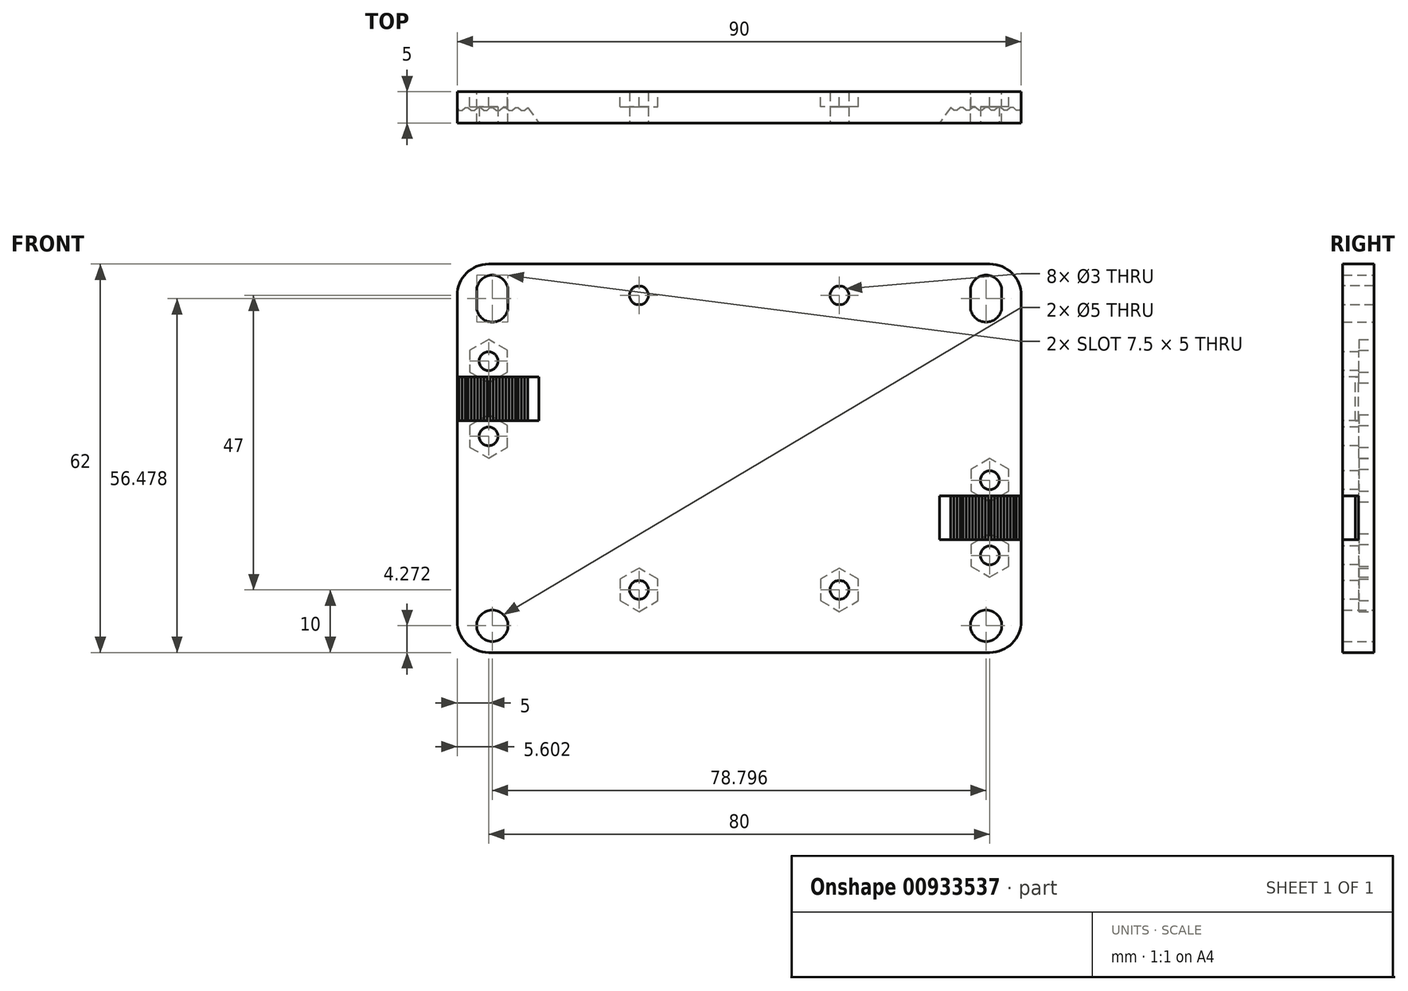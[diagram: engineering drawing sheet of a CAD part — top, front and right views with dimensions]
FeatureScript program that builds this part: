
annotation { "Feature Type Name" : "Feature", "Feature Type Description" : "" }
export const myFeature = defineFeature(function(context is Context, id is Id, definition is map)
    precondition{}
    {
        {
            var Q0;
            Q0=qCreatedBy(makeId("Front.planeOp"),FACE);
            var sketch = newSketch(context, id + "F0", { "sketchPlane" : qUnion([Q0])});
            skLineSegment(sketch, "E0.bottom", {"start": v(5, 0) * mm, "end": v(85, 0) * mm});
            skLineSegment(sketch, "E0.top", {"start": v(5, 62) * mm, "end": v(85, 62) * mm});
            skLineSegment(sketch, "E0.left", {"start": v(0, 5) * mm, "end": v(0, 57) * mm});
            skLineSegment(sketch, "E0.right", {"start": v(90, 5) * mm, "end": v(90, 57) * mm});
            skPoint(sketch, "E1.visualSharp", {"position": v(0, 62) * mm});
            skArc(sketch, "E1.filletArc", {"start": v(5, 62) * mm, "mid": v(1.46, 60.54) * mm, "end": v(0, 57) * mm});
            skPoint(sketch, "E2.visualSharp", {"position": v(90, 62) * mm});
            skArc(sketch, "E2.filletArc", {"start": v(90, 57) * mm, "mid": v(88.54, 60.54) * mm, "end": v(85, 62) * mm});
            skPoint(sketch, "E3.visualSharp", {"position": v(90, 0) * mm});
            skArc(sketch, "E3.filletArc", {"start": v(85, 0) * mm, "mid": v(88.54, 1.46) * mm, "end": v(90, 5) * mm});
            skPoint(sketch, "E4.visualSharp", {"position": v(0, 0) * mm});
            skArc(sketch, "E4.filletArc", {"start": v(0, 5) * mm, "mid": v(1.46, 1.46) * mm, "end": v(5, 0) * mm});
            skLineSegment(sketch, "E5", {"start": v(1.46, 60.54) * mm, "end": v(88.54, 1.46) * mm, "construction": true});
            skLineSegment(sketch, "E6", {"start": v(88.54, 1.46) * mm, "end": v(88.54, 60.54) * mm, "construction": true});
            skLineSegment(sketch, "E7", {"start": v(88.54, 60.54) * mm, "end": v(1.46, 1.46) * mm, "construction": true});
            skLineSegment(sketch, "E8", {"start": v(1.46, 1.46) * mm, "end": v(1.46, 60.54) * mm, "construction": true});
            skLineSegment(sketch, "E9", {"start": v(0, 31) * mm, "end": v(90, 31) * mm, "construction": true});
            skLineSegment(sketch, "E10", {"start": v(45, 62) * mm, "end": v(45, 0) * mm, "construction": true});
            skLineSegment(sketch, "E11", {"start": v(88.54, 60.54) * mm, "end": v(84.4, 57.73) * mm, "construction": true});
            skLineSegment(sketch, "E12", {"start": v(88.54, 1.46) * mm, "end": v(84.4, 4.27) * mm, "construction": true});
            skArc(sketch, "E13", {"start": v(86.9, 57.73) * mm, "mid": v(84.4, 60.23) * mm, "end": v(81.9, 57.73) * mm});
            skCircle(sketch, "E14", {"center": v(84.4, 4.27) * mm, "radius": 2.5 * mm});
            skCircle(sketch, "E15.MirrorC", {"center": v(5.6, 4.27) * mm, "radius": 2.5 * mm});
            skLineSegment(sketch, "E16", {"start": v(84.4, 57.73) * mm, "end": v(84.4, 55.23) * mm, "construction": true});
            skLineSegment(sketch, "E17", {"start": v(81.9, 57.73) * mm, "end": v(86.9, 57.73) * mm, "construction": true});
            skLineSegment(sketch, "E18", {"start": v(86.9, 55.23) * mm, "end": v(81.9, 55.23) * mm, "construction": true});
            skLineSegment(sketch, "E19", {"start": v(81.9, 57.73) * mm, "end": v(81.9, 55.23) * mm});
            skLineSegment(sketch, "E20", {"start": v(86.9, 57.73) * mm, "end": v(86.9, 55.23) * mm});
            skArc(sketch, "E21.trimOffspring", {"start": v(81.9, 55.23) * mm, "mid": v(84.4, 52.73) * mm, "end": v(86.9, 55.23) * mm});
            skLineSegment(sketch, "E22.MirrorCS", {"start": v(5.6, 57.73) * mm, "end": v(5.6, 55.23) * mm, "construction": true});
            skLineSegment(sketch, "E23.MirrorCS", {"start": v(3.1, 57.73) * mm, "end": v(3.1, 55.23) * mm});
            skArc(sketch, "E24.MirrorCS", {"start": v(8.1, 55.23) * mm, "mid": v(5.6, 52.73) * mm, "end": v(3.1, 55.23) * mm});
            skLineSegment(sketch, "E25.MirrorCS", {"start": v(8.1, 57.73) * mm, "end": v(3.1, 57.73) * mm, "construction": true});
            skArc(sketch, "E26.MirrorCS", {"start": v(3.1, 57.73) * mm, "mid": v(5.6, 60.23) * mm, "end": v(8.1, 57.73) * mm});
            skLineSegment(sketch, "E27.MirrorCS", {"start": v(8.1, 57.73) * mm, "end": v(8.1, 55.23) * mm});
            skLineSegment(sketch, "E28.MirrorCS", {"start": v(3.1, 55.23) * mm, "end": v(8.1, 55.23) * mm, "construction": true});
            skSolve(sketch);
        }
        {
            var Q0;
            Q0=makeQuery(id+"F0.imprint","IMPRINT",FACE,{"disambiguationData":[TD([[makeQuery(id+"F0.imprint","IMPRINT",EDGE,{"derivedFrom":sQuery(id+"F0.wireOp",EDGE,"E0.bottom")}),1.0]])]});
            extrude(context, id + "F1", {"entities" : qUnion([Q0]), "depth" : 5 * mm, "offsetDistance" : 25 * mm});
        }
        {
            var Q0;
            Q0=makeQuery(id+"F1.opExtrude","CAP_FACE",FACE,{"disambiguationData":[OSD([sQuery(id+"F0.wireOp",EDGE,"E0.bottom"),sQuery(id+"F0.wireOp",EDGE,"E0.top"),sQuery(id+"F0.wireOp",EDGE,"E0.left"),sQuery(id+"F0.wireOp",EDGE,"E0.right"),sQuery(id+"F0.wireOp",EDGE,"E1.filletArc"),sQuery(id+"F0.wireOp",EDGE,"E2.filletArc"),sQuery(id+"F0.wireOp",EDGE,"E3.filletArc"),sQuery(id+"F0.wireOp",EDGE,"E4.filletArc"),sQuery(id+"F0.wireOp",EDGE,"E13"),sQuery(id+"F0.wireOp",EDGE,"E14"),sQuery(id+"F0.wireOp",EDGE,"E15.MirrorC"),sQuery(id+"F0.wireOp",EDGE,"E19"),sQuery(id+"F0.wireOp",EDGE,"E20"),sQuery(id+"F0.wireOp",EDGE,"E21.trimOffspring"),sQuery(id+"F0.wireOp",EDGE,"E23.MirrorCS"),sQuery(id+"F0.wireOp",EDGE,"E24.MirrorCS"),sQuery(id+"F0.wireOp",EDGE,"E26.MirrorCS"),sQuery(id+"F0.wireOp",EDGE,"E27.MirrorCS")])],"isStart":false});
            var sketch = newSketch(context, id + "F2", { "sketchPlane" : qUnion([Q0])});
            skLineSegment(sketch, "E29", {"start": v(9.26, 62) * mm, "end": v(9.26, 44) * mm, "construction": true});
            skLineSegment(sketch, "E30", {"start": v(81.08, 0) * mm, "end": v(81.08, 18) * mm, "construction": true});
            skLineSegment(sketch, "E31.bottom", {"start": v(90, 18) * mm, "end": v(77, 18) * mm});
            skLineSegment(sketch, "E31.top", {"start": v(90, 25) * mm, "end": v(77, 25) * mm});
            skLineSegment(sketch, "E31.left", {"start": v(90, 18) * mm, "end": v(90, 25) * mm});
            skLineSegment(sketch, "E31.right", {"start": v(77, 18) * mm, "end": v(77, 25) * mm});
            skLineSegment(sketch, "E32.bottom", {"start": v(0, 44) * mm, "end": v(13, 44) * mm});
            skLineSegment(sketch, "E32.top", {"start": v(0, 37) * mm, "end": v(13, 37) * mm});
            skLineSegment(sketch, "E32.left", {"start": v(0, 44) * mm, "end": v(0, 37) * mm});
            skLineSegment(sketch, "E32.right", {"start": v(13, 44) * mm, "end": v(13, 37) * mm});
            skSolve(sketch);
        }
        {
            var Q0;
            Q0=makeQuery(id+"F2.imprint","IMPRINT",FACE,{"disambiguationData":[TD([[makeQuery(id+"F2.imprint","IMPRINT",EDGE,{"derivedFrom":sQuery(id+"F2.wireOp",EDGE,"E32.bottom")}),-1.0]])]});
            var Q1;
            Q1=makeQuery(id+"F2.imprint","IMPRINT",FACE,{"disambiguationData":[TD([[makeQuery(id+"F2.imprint","IMPRINT",EDGE,{"derivedFrom":sQuery(id+"F2.wireOp",EDGE,"E31.bottom")}),-1.0]])]});
            extrude(context, id + "F3", {"entities" : qUnion([Q0, Q1]), "operationType" : NewBodyOperationType.REMOVE, "oppositeDirection" : true, "depth" : 2.5 * mm, "offsetDistance" : 25 * mm});
        }
        {
            var Q0;
            Q0=makeQuery(id+"F3.boolean.opBoolean","COPY",FACE,{"derivedFrom":makeQuery(id+"F3.opExtrude","SWEPT_FACE",FACE,{"disambiguationData":[OSD([sQuery(id+"F2.wireOp",EDGE,"E32.bottom")])]})});
            var sketch = newSketch(context, id + "F4", { "sketchPlane" : qUnion([Q0])});
            skLineSegment(sketch, "E33", {"start": v(0, 2.5) * mm, "end": v(0, 3) * mm, "construction": true});
            skLineSegment(sketch, "E34", {"start": v(0, 3) * mm, "end": v(0.25, 3) * mm, "construction": true});
            skLineSegment(sketch, "E35", {"start": v(0.25, 3) * mm, "end": v(0.75, 3) * mm, "construction": true});
            skLineSegment(sketch, "E36", {"start": v(0.75, 3) * mm, "end": v(1.25, 3) * mm, "construction": true});
            skLineSegment(sketch, "E37", {"start": v(1.25, 3) * mm, "end": v(1.75, 3) * mm, "construction": true});
            skLineSegment(sketch, "E38", {"start": v(0, 2.5) * mm, "end": v(0.25, 3) * mm});
            skLineSegment(sketch, "E39", {"start": v(0.25, 3) * mm, "end": v(0.75, 3) * mm});
            skLineSegment(sketch, "E40", {"start": v(0.75, 3) * mm, "end": v(1.25, 2.5) * mm});
            skLineSegment(sketch, "E41", {"start": v(1.75, 3) * mm, "end": v(2.25, 3) * mm, "construction": true});
            skLineSegment(sketch, "E42", {"start": v(2.25, 3) * mm, "end": v(2.75, 3) * mm, "construction": true});
            skLineSegment(sketch, "E43", {"start": v(2.75, 3) * mm, "end": v(3.25, 3) * mm, "construction": true});
            skLineSegment(sketch, "E44", {"start": v(3.25, 3) * mm, "end": v(3.75, 3) * mm, "construction": true});
            skLineSegment(sketch, "E45", {"start": v(3.75, 3) * mm, "end": v(4.25, 3) * mm, "construction": true});
            skLineSegment(sketch, "E46", {"start": v(4.25, 3) * mm, "end": v(4.75, 3) * mm, "construction": true});
            skLineSegment(sketch, "E47", {"start": v(4.75, 3) * mm, "end": v(5.25, 3) * mm, "construction": true});
            skLineSegment(sketch, "E48", {"start": v(5.25, 3) * mm, "end": v(5.75, 3) * mm, "construction": true});
            skLineSegment(sketch, "E49", {"start": v(5.75, 3) * mm, "end": v(6.25, 3) * mm, "construction": true});
            skLineSegment(sketch, "E50", {"start": v(6.25, 3) * mm, "end": v(6.75, 3) * mm, "construction": true});
            skLineSegment(sketch, "E51", {"start": v(6.75, 3) * mm, "end": v(7.25, 3) * mm, "construction": true});
            skLineSegment(sketch, "E52", {"start": v(7.25, 3) * mm, "end": v(7.75, 3) * mm, "construction": true});
            skLineSegment(sketch, "E53", {"start": v(7.75, 3) * mm, "end": v(8.25, 3) * mm, "construction": true});
            skLineSegment(sketch, "E54", {"start": v(8.25, 3) * mm, "end": v(8.75, 3) * mm, "construction": true});
            skLineSegment(sketch, "E55", {"start": v(8.75, 3) * mm, "end": v(9.25, 3) * mm, "construction": true});
            skLineSegment(sketch, "E56", {"start": v(9.25, 3) * mm, "end": v(9.75, 3) * mm, "construction": true});
            skLineSegment(sketch, "E57", {"start": v(9.75, 3) * mm, "end": v(10.25, 3) * mm, "construction": true});
            skLineSegment(sketch, "E58", {"start": v(10.25, 3) * mm, "end": v(10.75, 3) * mm, "construction": true});
            skLineSegment(sketch, "E59", {"start": v(10.75, 3) * mm, "end": v(11.25, 3) * mm, "construction": true});
            skLineSegment(sketch, "E60", {"start": v(11.25, 3) * mm, "end": v(11.75, 3) * mm, "construction": true});
            skLineSegment(sketch, "E61", {"start": v(1.25, 2.5) * mm, "end": v(1.75, 2.5) * mm});
            skLineSegment(sketch, "E62", {"start": v(1.75, 2.5) * mm, "end": v(2.25, 3) * mm});
            skLineSegment(sketch, "E63", {"start": v(2.25, 3) * mm, "end": v(2.75, 3) * mm});
            skLineSegment(sketch, "E64", {"start": v(2.75, 3) * mm, "end": v(3.25, 2.5) * mm});
            skLineSegment(sketch, "E65", {"start": v(3.25, 2.5) * mm, "end": v(3.75, 2.5) * mm});
            skLineSegment(sketch, "E66", {"start": v(3.75, 2.5) * mm, "end": v(4.25, 3) * mm});
            skLineSegment(sketch, "E67", {"start": v(4.25, 3) * mm, "end": v(4.75, 3) * mm});
            skLineSegment(sketch, "E68", {"start": v(4.75, 3) * mm, "end": v(5.25, 2.5) * mm});
            skLineSegment(sketch, "E69", {"start": v(5.25, 2.5) * mm, "end": v(5.75, 2.5) * mm});
            skLineSegment(sketch, "E70", {"start": v(5.75, 2.5) * mm, "end": v(6.25, 3) * mm});
            skLineSegment(sketch, "E71", {"start": v(6.25, 3) * mm, "end": v(6.75, 3) * mm});
            skLineSegment(sketch, "E72", {"start": v(6.75, 3) * mm, "end": v(7.25, 2.5) * mm});
            skLineSegment(sketch, "E73", {"start": v(7.25, 2.5) * mm, "end": v(7.75, 2.5) * mm});
            skLineSegment(sketch, "E74", {"start": v(7.75, 2.5) * mm, "end": v(8.25, 3) * mm});
            skLineSegment(sketch, "E75", {"start": v(8.25, 3) * mm, "end": v(8.75, 3) * mm});
            skLineSegment(sketch, "E76", {"start": v(8.75, 3) * mm, "end": v(9.25, 2.5) * mm});
            skLineSegment(sketch, "E77", {"start": v(9.25, 2.5) * mm, "end": v(9.75, 2.5) * mm});
            skLineSegment(sketch, "E78", {"start": v(9.75, 2.5) * mm, "end": v(10.25, 3) * mm});
            skLineSegment(sketch, "E79", {"start": v(10.25, 3) * mm, "end": v(10.75, 3) * mm});
            skLineSegment(sketch, "E80", {"start": v(10.75, 3) * mm, "end": v(11.25, 2.5) * mm});
            skLineSegment(sketch, "E81", {"start": v(11.25, 2.5) * mm, "end": v(13, 5) * mm});
            skSolve(sketch);
        }
        {
            var Q0;
            {var subQ0=sQuery(id+"F4.wireOp",EDGE,"E81");Q0=makeQuery(id+"F4.imprint","IMPRINT",FACE,{"disambiguationData":[TD([[makeQuery(id+"F4.imprint","IMPRINT",EDGE,{"derivedFrom":subQ0}),-1.0]])]});}
            var Q1;
            {var subQ0=sQuery(id+"F4.wireOp",EDGE,"E74");Q1=makeQuery(id+"F4.imprint","IMPRINT",FACE,{"disambiguationData":[TD([[makeQuery(id+"F4.imprint","IMPRINT",EDGE,{"derivedFrom":subQ0}),-1.0]])]});}
            var Q2;
            {var subQ0=sQuery(id+"F4.wireOp",EDGE,"E78");Q2=makeQuery(id+"F4.imprint","IMPRINT",FACE,{"disambiguationData":[TD([[makeQuery(id+"F4.imprint","IMPRINT",EDGE,{"derivedFrom":subQ0}),-1.0]])]});}
            var Q3;
            {var subQ0=sQuery(id+"F4.wireOp",EDGE,"E70");Q3=makeQuery(id+"F4.imprint","IMPRINT",FACE,{"disambiguationData":[TD([[makeQuery(id+"F4.imprint","IMPRINT",EDGE,{"derivedFrom":subQ0}),-1.0]])]});}
            var Q4;
            {var subQ0=sQuery(id+"F4.wireOp",EDGE,"E66");Q4=makeQuery(id+"F4.imprint","IMPRINT",FACE,{"disambiguationData":[TD([[makeQuery(id+"F4.imprint","IMPRINT",EDGE,{"derivedFrom":subQ0}),-1.0]])]});}
            var Q5;
            {var subQ0=sQuery(id+"F4.wireOp",EDGE,"E62");Q5=makeQuery(id+"F4.imprint","IMPRINT",FACE,{"disambiguationData":[TD([[makeQuery(id+"F4.imprint","IMPRINT",EDGE,{"derivedFrom":subQ0}),-1.0]])]});}
            var Q6;
            {var subQ0=sQuery(id+"F4.wireOp",EDGE,"E38");Q6=makeQuery(id+"F4.imprint","IMPRINT",FACE,{"disambiguationData":[TD([[makeQuery(id+"F4.imprint","IMPRINT",EDGE,{"derivedFrom":subQ0}),-1.0]])]});}
            extrude(context, id + "F5", {"entities" : qUnion([Q0, Q1, Q2, Q3, Q4, Q5, Q6]), "operationType" : NewBodyOperationType.ADD, "endBound" : BoundingType.UP_TO_NEXT, "depth" : 25 * mm, "offsetDistance" : 25 * mm});
        }
        {
            var Q0;
            Q0=makeQuery(id+"F3.boolean.opBoolean","COPY",FACE,{"derivedFrom":makeQuery(id+"F3.opExtrude","SWEPT_FACE",FACE,{"disambiguationData":[OSD([sQuery(id+"F2.wireOp",EDGE,"E31.bottom")])]})});
            var sketch = newSketch(context, id + "F6", { "sketchPlane" : qUnion([Q0])});
            skLineSegment(sketch, "E82", {"start": v(90, -2.5) * mm, "end": v(90, -3) * mm, "construction": true});
            skLineSegment(sketch, "E83", {"start": v(90, -3) * mm, "end": v(89.75, -3) * mm, "construction": true});
            skLineSegment(sketch, "E84", {"start": v(89.75, -3) * mm, "end": v(89.25, -3) * mm, "construction": true});
            skLineSegment(sketch, "E85", {"start": v(89.25, -3) * mm, "end": v(88.75, -3) * mm, "construction": true});
            skLineSegment(sketch, "E86", {"start": v(88.75, -3) * mm, "end": v(88.25, -3) * mm, "construction": true});
            skLineSegment(sketch, "E87", {"start": v(88.25, -3) * mm, "end": v(87.75, -3) * mm, "construction": true});
            skLineSegment(sketch, "E88", {"start": v(87.75, -3) * mm, "end": v(87.25, -3) * mm, "construction": true});
            skLineSegment(sketch, "E89", {"start": v(87.25, -3) * mm, "end": v(86.75, -3) * mm, "construction": true});
            skLineSegment(sketch, "E90", {"start": v(86.75, -3) * mm, "end": v(86.25, -3) * mm, "construction": true});
            skLineSegment(sketch, "E91", {"start": v(86.25, -3) * mm, "end": v(85.75, -3) * mm, "construction": true});
            skLineSegment(sketch, "E92", {"start": v(85.75, -3) * mm, "end": v(85.25, -3) * mm, "construction": true});
            skLineSegment(sketch, "E93", {"start": v(85.25, -3) * mm, "end": v(84.75, -3) * mm, "construction": true});
            skLineSegment(sketch, "E94", {"start": v(84.75, -3) * mm, "end": v(84.25, -3) * mm, "construction": true});
            skLineSegment(sketch, "E95", {"start": v(84.25, -3) * mm, "end": v(83.75, -3) * mm, "construction": true});
            skLineSegment(sketch, "E96", {"start": v(83.75, -3) * mm, "end": v(83.25, -3) * mm, "construction": true});
            skLineSegment(sketch, "E97", {"start": v(83.25, -3) * mm, "end": v(82.75, -3) * mm, "construction": true});
            skLineSegment(sketch, "E98", {"start": v(82.75, -3) * mm, "end": v(82.25, -3) * mm, "construction": true});
            skLineSegment(sketch, "E99", {"start": v(82.25, -3) * mm, "end": v(81.75, -3) * mm, "construction": true});
            skLineSegment(sketch, "E100", {"start": v(81.75, -3) * mm, "end": v(81.25, -3) * mm, "construction": true});
            skLineSegment(sketch, "E101", {"start": v(81.25, -3) * mm, "end": v(80.75, -3) * mm, "construction": true});
            skLineSegment(sketch, "E102", {"start": v(80.75, -3) * mm, "end": v(80.25, -3) * mm, "construction": true});
            skLineSegment(sketch, "E103", {"start": v(80.25, -3) * mm, "end": v(79.75, -3) * mm, "construction": true});
            skLineSegment(sketch, "E104", {"start": v(79.75, -3) * mm, "end": v(79.25, -3) * mm, "construction": true});
            skLineSegment(sketch, "E105", {"start": v(79.25, -3) * mm, "end": v(78.75, -3) * mm, "construction": true});
            skLineSegment(sketch, "E106", {"start": v(78.75, -3) * mm, "end": v(78.25, -3) * mm, "construction": true});
            skLineSegment(sketch, "E107", {"start": v(78.25, -3) * mm, "end": v(77.75, -3) * mm, "construction": true});
            skLineSegment(sketch, "E108", {"start": v(90, -2.5) * mm, "end": v(89.75, -3) * mm});
            skLineSegment(sketch, "E109", {"start": v(89.75, -3) * mm, "end": v(89.25, -3) * mm});
            skLineSegment(sketch, "E110", {"start": v(89.25, -3) * mm, "end": v(88.75, -2.5) * mm});
            skLineSegment(sketch, "E111", {"start": v(88.75, -2.5) * mm, "end": v(88.25, -2.5) * mm});
            skLineSegment(sketch, "E112", {"start": v(88.25, -2.5) * mm, "end": v(87.75, -3) * mm});
            skLineSegment(sketch, "E113", {"start": v(87.75, -3) * mm, "end": v(87.25, -3) * mm});
            skLineSegment(sketch, "E114", {"start": v(87.25, -3) * mm, "end": v(86.75, -2.5) * mm});
            skLineSegment(sketch, "E115", {"start": v(86.75, -2.5) * mm, "end": v(86.25, -2.5) * mm});
            skLineSegment(sketch, "E116", {"start": v(86.25, -2.5) * mm, "end": v(85.75, -3) * mm});
            skLineSegment(sketch, "E117", {"start": v(85.75, -3) * mm, "end": v(85.25, -3) * mm});
            skLineSegment(sketch, "E118", {"start": v(85.25, -3) * mm, "end": v(84.75, -2.5) * mm});
            skLineSegment(sketch, "E119", {"start": v(84.75, -2.5) * mm, "end": v(84.25, -2.5) * mm});
            skLineSegment(sketch, "E120", {"start": v(84.25, -2.5) * mm, "end": v(83.75, -3) * mm});
            skLineSegment(sketch, "E121", {"start": v(83.75, -3) * mm, "end": v(83.25, -3) * mm});
            skLineSegment(sketch, "E122", {"start": v(83.25, -3) * mm, "end": v(82.75, -2.5) * mm});
            skLineSegment(sketch, "E123", {"start": v(82.75, -2.5) * mm, "end": v(82.25, -2.5) * mm});
            skLineSegment(sketch, "E124", {"start": v(82.25, -2.5) * mm, "end": v(81.75, -3) * mm});
            skLineSegment(sketch, "E125", {"start": v(81.75, -3) * mm, "end": v(81.25, -3) * mm});
            skLineSegment(sketch, "E126", {"start": v(81.25, -3) * mm, "end": v(80.75, -2.5) * mm});
            skLineSegment(sketch, "E127", {"start": v(80.75, -2.5) * mm, "end": v(80.25, -2.5) * mm});
            skLineSegment(sketch, "E128", {"start": v(80.25, -2.5) * mm, "end": v(79.75, -3) * mm});
            skLineSegment(sketch, "E129", {"start": v(79.75, -3) * mm, "end": v(79.25, -3) * mm});
            skLineSegment(sketch, "E130", {"start": v(79.25, -3) * mm, "end": v(78.75, -2.5) * mm});
            skLineSegment(sketch, "E131", {"start": v(78.75, -2.5) * mm, "end": v(77, -5) * mm});
            skSolve(sketch);
        }
        {
            var Q0;
            {var subQ0=sQuery(id+"F6.wireOp",EDGE,"E131");Q0=makeQuery(id+"F6.imprint","IMPRINT",FACE,{"disambiguationData":[TD([[makeQuery(id+"F6.imprint","IMPRINT",EDGE,{"derivedFrom":subQ0}),-1.0]])]});}
            var Q1;
            {var subQ0=sQuery(id+"F6.wireOp",EDGE,"E128");Q1=makeQuery(id+"F6.imprint","IMPRINT",FACE,{"disambiguationData":[TD([[makeQuery(id+"F6.imprint","IMPRINT",EDGE,{"derivedFrom":subQ0}),-1.0]])]});}
            var Q2;
            {var subQ0=sQuery(id+"F6.wireOp",EDGE,"E124");Q2=makeQuery(id+"F6.imprint","IMPRINT",FACE,{"disambiguationData":[TD([[makeQuery(id+"F6.imprint","IMPRINT",EDGE,{"derivedFrom":subQ0}),-1.0]])]});}
            var Q3;
            {var subQ0=sQuery(id+"F6.wireOp",EDGE,"E120");Q3=makeQuery(id+"F6.imprint","IMPRINT",FACE,{"disambiguationData":[TD([[makeQuery(id+"F6.imprint","IMPRINT",EDGE,{"derivedFrom":subQ0}),-1.0]])]});}
            var Q4;
            {var subQ0=sQuery(id+"F6.wireOp",EDGE,"E116");Q4=makeQuery(id+"F6.imprint","IMPRINT",FACE,{"disambiguationData":[TD([[makeQuery(id+"F6.imprint","IMPRINT",EDGE,{"derivedFrom":subQ0}),-1.0]])]});}
            var Q5;
            {var subQ0=sQuery(id+"F6.wireOp",EDGE,"E112");Q5=makeQuery(id+"F6.imprint","IMPRINT",FACE,{"disambiguationData":[TD([[makeQuery(id+"F6.imprint","IMPRINT",EDGE,{"derivedFrom":subQ0}),-1.0]])]});}
            var Q6;
            {var subQ0=sQuery(id+"F6.wireOp",EDGE,"E108");Q6=makeQuery(id+"F6.imprint","IMPRINT",FACE,{"disambiguationData":[TD([[makeQuery(id+"F6.imprint","IMPRINT",EDGE,{"derivedFrom":subQ0}),-1.0]])]});}
            extrude(context, id + "F7", {"entities" : qUnion([Q0, Q1, Q2, Q3, Q4, Q5, Q6]), "operationType" : NewBodyOperationType.ADD, "endBound" : BoundingType.UP_TO_NEXT, "depth" : 25 * mm, "offsetDistance" : 25 * mm});
        }
        {
            var Q0;
            Q0=makeQuery(id+"F1.opExtrude","CAP_FACE",FACE,{"disambiguationData":[OSD([sQuery(id+"F0.wireOp",EDGE,"E0.bottom"),sQuery(id+"F0.wireOp",EDGE,"E0.top"),sQuery(id+"F0.wireOp",EDGE,"E0.left"),sQuery(id+"F0.wireOp",EDGE,"E0.right"),sQuery(id+"F0.wireOp",EDGE,"E1.filletArc"),sQuery(id+"F0.wireOp",EDGE,"E2.filletArc"),sQuery(id+"F0.wireOp",EDGE,"E3.filletArc"),sQuery(id+"F0.wireOp",EDGE,"E4.filletArc"),sQuery(id+"F0.wireOp",EDGE,"E13"),sQuery(id+"F0.wireOp",EDGE,"E14"),sQuery(id+"F0.wireOp",EDGE,"E15.MirrorC"),sQuery(id+"F0.wireOp",EDGE,"E19"),sQuery(id+"F0.wireOp",EDGE,"E20"),sQuery(id+"F0.wireOp",EDGE,"E21.trimOffspring"),sQuery(id+"F0.wireOp",EDGE,"E23.MirrorCS"),sQuery(id+"F0.wireOp",EDGE,"E24.MirrorCS"),sQuery(id+"F0.wireOp",EDGE,"E26.MirrorCS"),sQuery(id+"F0.wireOp",EDGE,"E27.MirrorCS")])],"isStart":false});
            var sketch = newSketch(context, id + "F8", { "sketchPlane" : qUnion([Q0])});
            skLineSegment(sketch, "E132", {"start": v(90, 29.82) * mm, "end": v(85, 29.82) * mm, "construction": true});
            skLineSegment(sketch, "E133", {"start": v(85, 25) * mm, "end": v(85, 27.5) * mm, "construction": true});
            skLineSegment(sketch, "E134", {"start": v(85, 18) * mm, "end": v(85, 15.5) * mm, "construction": true});
            skCircle(sketch, "E135", {"center": v(85, 27.5) * mm, "radius": 1.5 * mm});
            skCircle(sketch, "E136", {"center": v(85, 15.5) * mm, "radius": 1.5 * mm});
            skLineSegment(sketch, "E137", {"start": v(0, 51.21) * mm, "end": v(5, 51.21) * mm, "construction": true});
            skLineSegment(sketch, "E138", {"start": v(5, 44) * mm, "end": v(5, 46.5) * mm, "construction": true});
            skLineSegment(sketch, "E139", {"start": v(5, 37) * mm, "end": v(5, 34.5) * mm, "construction": true});
            skCircle(sketch, "E140", {"center": v(5, 46.5) * mm, "radius": 1.5 * mm});
            skCircle(sketch, "E141", {"center": v(5, 34.5) * mm, "radius": 1.5 * mm});
            skSolve(sketch);
        }
        {
            var Q0;
            Q0=makeQuery(id+"F8.imprint","IMPRINT",FACE,{"disambiguationData":[TD([[makeQuery(id+"F8.imprint","IMPRINT",EDGE,{"derivedFrom":sQuery(id+"F8.wireOp",EDGE,"E140")}),1.0]])]});
            var Q1;
            Q1=makeQuery(id+"F8.imprint","IMPRINT",FACE,{"disambiguationData":[TD([[makeQuery(id+"F8.imprint","IMPRINT",EDGE,{"derivedFrom":sQuery(id+"F8.wireOp",EDGE,"E141")}),1.0]])]});
            var Q2;
            Q2=makeQuery(id+"F8.imprint","IMPRINT",FACE,{"disambiguationData":[TD([[makeQuery(id+"F8.imprint","IMPRINT",EDGE,{"derivedFrom":sQuery(id+"F8.wireOp",EDGE,"E135")}),1.0]])]});
            var Q3;
            Q3=makeQuery(id+"F8.imprint","IMPRINT",FACE,{"disambiguationData":[TD([[makeQuery(id+"F8.imprint","IMPRINT",EDGE,{"derivedFrom":sQuery(id+"F8.wireOp",EDGE,"E136")}),1.0]])]});
            extrude(context, id + "F9", {"entities" : qUnion([Q0, Q1, Q2, Q3]), "operationType" : NewBodyOperationType.REMOVE, "oppositeDirection" : true, "depth" : 5 * mm, "offsetDistance" : 25 * mm});
        }
        {
            var Q0;
            Q0=makeQuery(id+"F1.opExtrude","CAP_FACE",FACE,{"disambiguationData":[OSD([sQuery(id+"F0.wireOp",EDGE,"E0.bottom"),sQuery(id+"F0.wireOp",EDGE,"E0.top"),sQuery(id+"F0.wireOp",EDGE,"E0.left"),sQuery(id+"F0.wireOp",EDGE,"E0.right"),sQuery(id+"F0.wireOp",EDGE,"E1.filletArc"),sQuery(id+"F0.wireOp",EDGE,"E2.filletArc"),sQuery(id+"F0.wireOp",EDGE,"E3.filletArc"),sQuery(id+"F0.wireOp",EDGE,"E4.filletArc"),sQuery(id+"F0.wireOp",EDGE,"E13"),sQuery(id+"F0.wireOp",EDGE,"E14"),sQuery(id+"F0.wireOp",EDGE,"E15.MirrorC"),sQuery(id+"F0.wireOp",EDGE,"E19"),sQuery(id+"F0.wireOp",EDGE,"E20"),sQuery(id+"F0.wireOp",EDGE,"E21.trimOffspring"),sQuery(id+"F0.wireOp",EDGE,"E23.MirrorCS"),sQuery(id+"F0.wireOp",EDGE,"E24.MirrorCS"),sQuery(id+"F0.wireOp",EDGE,"E26.MirrorCS"),sQuery(id+"F0.wireOp",EDGE,"E27.MirrorCS")])],"isStart":true});
            var sketch = newSketch(context, id + "F10", { "sketchPlane" : qUnion([Q0])});
            skLineSegment(sketch, "E142", {"start": v(-85, 27.5) * mm, "end": v(-82, 27.5) * mm, "construction": true});
            skLineSegment(sketch, "E143", {"start": v(-85, 15.5) * mm, "end": v(-82, 15.5) * mm, "construction": true});
            skLineSegment(sketch, "E144", {"start": v(-5, 46.5) * mm, "end": v(-8, 46.5) * mm, "construction": true});
            skLineSegment(sketch, "E145", {"start": v(-5, 34.5) * mm, "end": v(-8, 34.5) * mm, "construction": true});
            skCircle(sketch, "E146.cCircle", {"center": v(-5, 46.5) * mm, "radius": 3 * mm, "construction": true});
            skLineSegment(sketch, "E146.0", {"start": v(-8, 44.77) * mm, "end": v(-8, 48.23) * mm});
            skLineSegment(sketch, "E146.1", {"start": v(-8, 48.23) * mm, "end": v(-5, 49.96) * mm});
            skLineSegment(sketch, "E146.2", {"start": v(-5, 49.96) * mm, "end": v(-2, 48.23) * mm});
            skLineSegment(sketch, "E146.3", {"start": v(-2, 48.23) * mm, "end": v(-2, 44.77) * mm});
            skLineSegment(sketch, "E146.4", {"start": v(-2, 44.77) * mm, "end": v(-5, 43.04) * mm});
            skLineSegment(sketch, "E146.5", {"start": v(-5, 43.04) * mm, "end": v(-8, 44.77) * mm});
            skPoint(sketch, "E146.0.midPoint", {"position": v(-8, 46.5) * mm});
            skCircle(sketch, "E147.cCircle", {"center": v(-5, 34.5) * mm, "radius": 3 * mm, "construction": true});
            skLineSegment(sketch, "E147.0", {"start": v(-8, 32.77) * mm, "end": v(-8, 36.23) * mm});
            skLineSegment(sketch, "E147.1", {"start": v(-8, 36.23) * mm, "end": v(-5, 37.96) * mm});
            skLineSegment(sketch, "E147.2", {"start": v(-5, 37.96) * mm, "end": v(-2, 36.23) * mm});
            skLineSegment(sketch, "E147.3", {"start": v(-2, 36.23) * mm, "end": v(-2, 32.77) * mm});
            skLineSegment(sketch, "E147.4", {"start": v(-2, 32.77) * mm, "end": v(-5, 31.04) * mm});
            skLineSegment(sketch, "E147.5", {"start": v(-5, 31.04) * mm, "end": v(-8, 32.77) * mm});
            skPoint(sketch, "E147.0.midPoint", {"position": v(-8, 34.5) * mm});
            skCircle(sketch, "E148.cCircle", {"center": v(-85, 27.5) * mm, "radius": 3 * mm, "construction": true});
            skLineSegment(sketch, "E148.0", {"start": v(-82, 29.23) * mm, "end": v(-82, 25.77) * mm});
            skLineSegment(sketch, "E148.1", {"start": v(-82, 25.77) * mm, "end": v(-85, 24.04) * mm});
            skLineSegment(sketch, "E148.2", {"start": v(-85, 24.04) * mm, "end": v(-88, 25.77) * mm});
            skLineSegment(sketch, "E148.3", {"start": v(-88, 25.77) * mm, "end": v(-88, 29.23) * mm});
            skLineSegment(sketch, "E148.4", {"start": v(-88, 29.23) * mm, "end": v(-85, 30.96) * mm});
            skLineSegment(sketch, "E148.5", {"start": v(-85, 30.96) * mm, "end": v(-82, 29.23) * mm});
            skPoint(sketch, "E148.0.midPoint", {"position": v(-82, 27.5) * mm});
            skCircle(sketch, "E149.cCircle", {"center": v(-85, 15.5) * mm, "radius": 3 * mm, "construction": true});
            skLineSegment(sketch, "E149.0", {"start": v(-82, 17.23) * mm, "end": v(-82, 13.77) * mm});
            skLineSegment(sketch, "E149.1", {"start": v(-82, 13.77) * mm, "end": v(-85, 12.04) * mm});
            skLineSegment(sketch, "E149.2", {"start": v(-85, 12.04) * mm, "end": v(-88, 13.77) * mm});
            skLineSegment(sketch, "E149.3", {"start": v(-88, 13.77) * mm, "end": v(-88, 17.23) * mm});
            skLineSegment(sketch, "E149.4", {"start": v(-88, 17.23) * mm, "end": v(-85, 18.96) * mm});
            skLineSegment(sketch, "E149.5", {"start": v(-85, 18.96) * mm, "end": v(-82, 17.23) * mm});
            skPoint(sketch, "E149.0.midPoint", {"position": v(-82, 15.5) * mm});
            skSolve(sketch);
        }
        {
            var Q0;
            Q0=makeQuery(id+"F10.imprint","IMPRINT",FACE,{"disambiguationData":[TD([[makeQuery(id+"F10.imprint","IMPRINT",EDGE,{"derivedFrom":sQuery(id+"F10.wireOp",EDGE,"E148.0")}),-1.0]])]});
            var Q1;
            Q1=makeQuery(id+"F10.imprint","IMPRINT",FACE,{"disambiguationData":[TD([[makeQuery(id+"F10.imprint","IMPRINT",EDGE,{"derivedFrom":sQuery(id+"F10.wireOp",EDGE,"E149.0")}),-1.0]])]});
            var Q2;
            Q2=makeQuery(id+"F10.imprint","IMPRINT",FACE,{"disambiguationData":[TD([[makeQuery(id+"F10.imprint","IMPRINT",EDGE,{"derivedFrom":sQuery(id+"F10.wireOp",EDGE,"E147.0")}),-1.0]])]});
            var Q3;
            Q3=makeQuery(id+"F10.imprint","IMPRINT",FACE,{"disambiguationData":[TD([[makeQuery(id+"F10.imprint","IMPRINT",EDGE,{"derivedFrom":sQuery(id+"F10.wireOp",EDGE,"E146.0")}),-1.0]])]});
            extrude(context, id + "F11", {"entities" : qUnion([Q0, Q1, Q2, Q3]), "operationType" : NewBodyOperationType.REMOVE, "oppositeDirection" : true, "depth" : 2.4 * mm, "offsetDistance" : 25 * mm});
        }
        {
            var Q0;
            Q0=makeQuery(id+"F1.opExtrude","CAP_FACE",FACE,{"disambiguationData":[OSD([sQuery(id+"F0.wireOp",EDGE,"E0.bottom"),sQuery(id+"F0.wireOp",EDGE,"E0.top"),sQuery(id+"F0.wireOp",EDGE,"E0.left"),sQuery(id+"F0.wireOp",EDGE,"E0.right"),sQuery(id+"F0.wireOp",EDGE,"E1.filletArc"),sQuery(id+"F0.wireOp",EDGE,"E2.filletArc"),sQuery(id+"F0.wireOp",EDGE,"E3.filletArc"),sQuery(id+"F0.wireOp",EDGE,"E4.filletArc"),sQuery(id+"F0.wireOp",EDGE,"E13"),sQuery(id+"F0.wireOp",EDGE,"E14"),sQuery(id+"F0.wireOp",EDGE,"E15.MirrorC"),sQuery(id+"F0.wireOp",EDGE,"E19"),sQuery(id+"F0.wireOp",EDGE,"E20"),sQuery(id+"F0.wireOp",EDGE,"E21.trimOffspring"),sQuery(id+"F0.wireOp",EDGE,"E23.MirrorCS"),sQuery(id+"F0.wireOp",EDGE,"E24.MirrorCS"),sQuery(id+"F0.wireOp",EDGE,"E26.MirrorCS"),sQuery(id+"F0.wireOp",EDGE,"E27.MirrorCS")])],"isStart":false});
            var sketch = newSketch(context, id + "F12", { "sketchPlane" : qUnion([Q0])});
            skLineSegment(sketch, "E150", {"start": v(45, 0) * mm, "end": v(45, 10) * mm, "construction": true});
            skLineSegment(sketch, "E151", {"start": v(45, 10) * mm, "end": v(61, 10) * mm, "construction": true});
            skLineSegment(sketch, "E152", {"start": v(45, 10) * mm, "end": v(29, 10) * mm, "construction": true});
            skLineSegment(sketch, "E153", {"start": v(45, 62) * mm, "end": v(45, 57) * mm, "construction": true});
            skLineSegment(sketch, "E154", {"start": v(45, 57) * mm, "end": v(61, 57) * mm, "construction": true});
            skLineSegment(sketch, "E155", {"start": v(45, 57) * mm, "end": v(29, 57) * mm, "construction": true});
            skCircle(sketch, "E156", {"center": v(29, 10) * mm, "radius": 1.5 * mm});
            skCircle(sketch, "E157", {"center": v(61, 10) * mm, "radius": 1.5 * mm});
            skCircle(sketch, "E158", {"center": v(61, 57) * mm, "radius": 1.5 * mm});
            skCircle(sketch, "E159", {"center": v(29, 57) * mm, "radius": 1.5 * mm});
            skSolve(sketch);
        }
        {
            var Q0;
            Q0=makeQuery(id+"F12.imprint","IMPRINT",FACE,{"disambiguationData":[TD([[makeQuery(id+"F12.imprint","IMPRINT",EDGE,{"derivedFrom":sQuery(id+"F12.wireOp",EDGE,"E158")}),1.0]])]});
            var Q1;
            Q1=makeQuery(id+"F12.imprint","IMPRINT",FACE,{"disambiguationData":[TD([[makeQuery(id+"F12.imprint","IMPRINT",EDGE,{"derivedFrom":sQuery(id+"F12.wireOp",EDGE,"E159")}),1.0]])]});
            var Q2;
            Q2=makeQuery(id+"F12.imprint","IMPRINT",FACE,{"disambiguationData":[TD([[makeQuery(id+"F12.imprint","IMPRINT",EDGE,{"derivedFrom":sQuery(id+"F12.wireOp",EDGE,"E156")}),1.0]])]});
            var Q3;
            Q3=makeQuery(id+"F12.imprint","IMPRINT",FACE,{"disambiguationData":[TD([[makeQuery(id+"F12.imprint","IMPRINT",EDGE,{"derivedFrom":sQuery(id+"F12.wireOp",EDGE,"E157")}),1.0]])]});
            extrude(context, id + "F13", {"entities" : qUnion([Q0, Q1, Q2, Q3]), "operationType" : NewBodyOperationType.REMOVE, "oppositeDirection" : true, "depth" : 5 * mm, "offsetDistance" : 25 * mm});
        }
        {
            var Q0;
            Q0=makeQuery(id+"F1.opExtrude","CAP_FACE",FACE,{"disambiguationData":[OSD([sQuery(id+"F0.wireOp",EDGE,"E0.bottom"),sQuery(id+"F0.wireOp",EDGE,"E0.top"),sQuery(id+"F0.wireOp",EDGE,"E0.left"),sQuery(id+"F0.wireOp",EDGE,"E0.right"),sQuery(id+"F0.wireOp",EDGE,"E1.filletArc"),sQuery(id+"F0.wireOp",EDGE,"E2.filletArc"),sQuery(id+"F0.wireOp",EDGE,"E3.filletArc"),sQuery(id+"F0.wireOp",EDGE,"E4.filletArc"),sQuery(id+"F0.wireOp",EDGE,"E13"),sQuery(id+"F0.wireOp",EDGE,"E14"),sQuery(id+"F0.wireOp",EDGE,"E15.MirrorC"),sQuery(id+"F0.wireOp",EDGE,"E19"),sQuery(id+"F0.wireOp",EDGE,"E20"),sQuery(id+"F0.wireOp",EDGE,"E21.trimOffspring"),sQuery(id+"F0.wireOp",EDGE,"E23.MirrorCS"),sQuery(id+"F0.wireOp",EDGE,"E24.MirrorCS"),sQuery(id+"F0.wireOp",EDGE,"E26.MirrorCS"),sQuery(id+"F0.wireOp",EDGE,"E27.MirrorCS")])],"isStart":true});
            var sketch = newSketch(context, id + "F14", { "sketchPlane" : qUnion([Q0])});
            skLineSegment(sketch, "E160", {"start": v(-61, 10) * mm, "end": v(-58, 10) * mm, "construction": true});
            skLineSegment(sketch, "E161", {"start": v(-29, 10) * mm, "end": v(-32, 10) * mm, "construction": true});
            skCircle(sketch, "E162.cCircle", {"center": v(-61, 10) * mm, "radius": 3 * mm, "construction": true});
            skLineSegment(sketch, "E162.0", {"start": v(-58, 11.73) * mm, "end": v(-58, 8.27) * mm});
            skLineSegment(sketch, "E162.1", {"start": v(-58, 8.27) * mm, "end": v(-61, 6.54) * mm});
            skLineSegment(sketch, "E162.2", {"start": v(-61, 6.54) * mm, "end": v(-64, 8.27) * mm});
            skLineSegment(sketch, "E162.3", {"start": v(-64, 8.27) * mm, "end": v(-64, 11.73) * mm});
            skLineSegment(sketch, "E162.4", {"start": v(-64, 11.73) * mm, "end": v(-61, 13.46) * mm});
            skLineSegment(sketch, "E162.5", {"start": v(-61, 13.46) * mm, "end": v(-58, 11.73) * mm});
            skPoint(sketch, "E162.0.midPoint", {"position": v(-58, 10) * mm});
            skCircle(sketch, "E163.cCircle", {"center": v(-29, 10) * mm, "radius": 3 * mm, "construction": true});
            skLineSegment(sketch, "E163.0", {"start": v(-32, 8.27) * mm, "end": v(-32, 11.73) * mm});
            skLineSegment(sketch, "E163.1", {"start": v(-32, 11.73) * mm, "end": v(-29, 13.46) * mm});
            skLineSegment(sketch, "E163.2", {"start": v(-29, 13.46) * mm, "end": v(-26, 11.73) * mm});
            skLineSegment(sketch, "E163.3", {"start": v(-26, 11.73) * mm, "end": v(-26, 8.27) * mm});
            skLineSegment(sketch, "E163.4", {"start": v(-26, 8.27) * mm, "end": v(-29, 6.54) * mm});
            skLineSegment(sketch, "E163.5", {"start": v(-29, 6.54) * mm, "end": v(-32, 8.27) * mm});
            skPoint(sketch, "E163.0.midPoint", {"position": v(-32, 10) * mm});
            skSolve(sketch);
        }
        {
            var Q0;
            Q0=makeQuery(id+"F14.imprint","IMPRINT",FACE,{"disambiguationData":[TD([[makeQuery(id+"F14.imprint","IMPRINT",EDGE,{"derivedFrom":sQuery(id+"F14.wireOp",EDGE,"E162.0")}),-1.0]])]});
            var Q1;
            Q1=makeQuery(id+"F14.imprint","IMPRINT",FACE,{"disambiguationData":[TD([[makeQuery(id+"F14.imprint","IMPRINT",EDGE,{"derivedFrom":sQuery(id+"F14.wireOp",EDGE,"E163.0")}),-1.0]])]});
            extrude(context, id + "F15", {"entities" : qUnion([Q0, Q1]), "operationType" : NewBodyOperationType.REMOVE, "oppositeDirection" : true, "depth" : 2.4 * mm, "offsetDistance" : 25 * mm});
        }
    });
